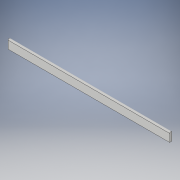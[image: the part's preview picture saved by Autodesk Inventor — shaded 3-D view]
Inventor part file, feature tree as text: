
AUTODESK INVENTOR PART (.ipt)
format: ipt  version: 2019 (Build 230136000, 136)  size: 99,840 bytes
history: native  units: mm
features: other x1, extrude x1, fillet x1, sketch x1
ambient origin geometry x8: Origin, YZ Plane, XZ Plane, XY Plane, X Axis, Y Axis, Z Axis, Center Point
bodies: Body1 (feature_tree)
feature tree (4):
  other  "Bryła1"
  extrude  "Wyciągnięcie proste1"  Depth=4.0mm
  fillet  "Zaokrąglenie1"  Radius=72.4mm
  sketch  "Szkic1"
